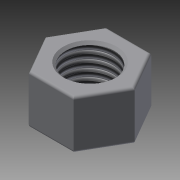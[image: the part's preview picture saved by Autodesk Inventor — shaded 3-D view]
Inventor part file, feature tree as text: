
AUTODESK INVENTOR PART (.ipt)
format: ipt  version: 2015 (Build 190159000, 159)  size: 111,616 bytes
history: native  units: mm
features: extrude x1, thread x1, fillet x1, chamfer x1, sketch x1
ambient origin geometry x8: Origin, YZ Plane, XZ Plane, XY Plane, X Axis, Y Axis, Z Axis, Center Point
bodies: 实体1 (feature_tree)
feature tree (5):
  extrude  "拉伸1"  Depth=0.25mm
  thread  "螺纹1"  [1 undecoded]
  fillet  "圆角1"  Radius=5.0mm
  chamfer  "倒角1"  Distance=10.0mm
  sketch  "草图1"  dims[d0=5.0mm d1=1.539821mm d2=8.0mm d3=5.0mm d4=0.0mm d5=10.0mm d6=0.0mm d7=0.25mm d8=0.25mm d9=2.0mm d10=45.0deg]
note: 1 required parameter value undecoded (feature->parameter linkage not recoverable at this tier; creation-order binding heuristic only, values carry confidence <= 0.55)
